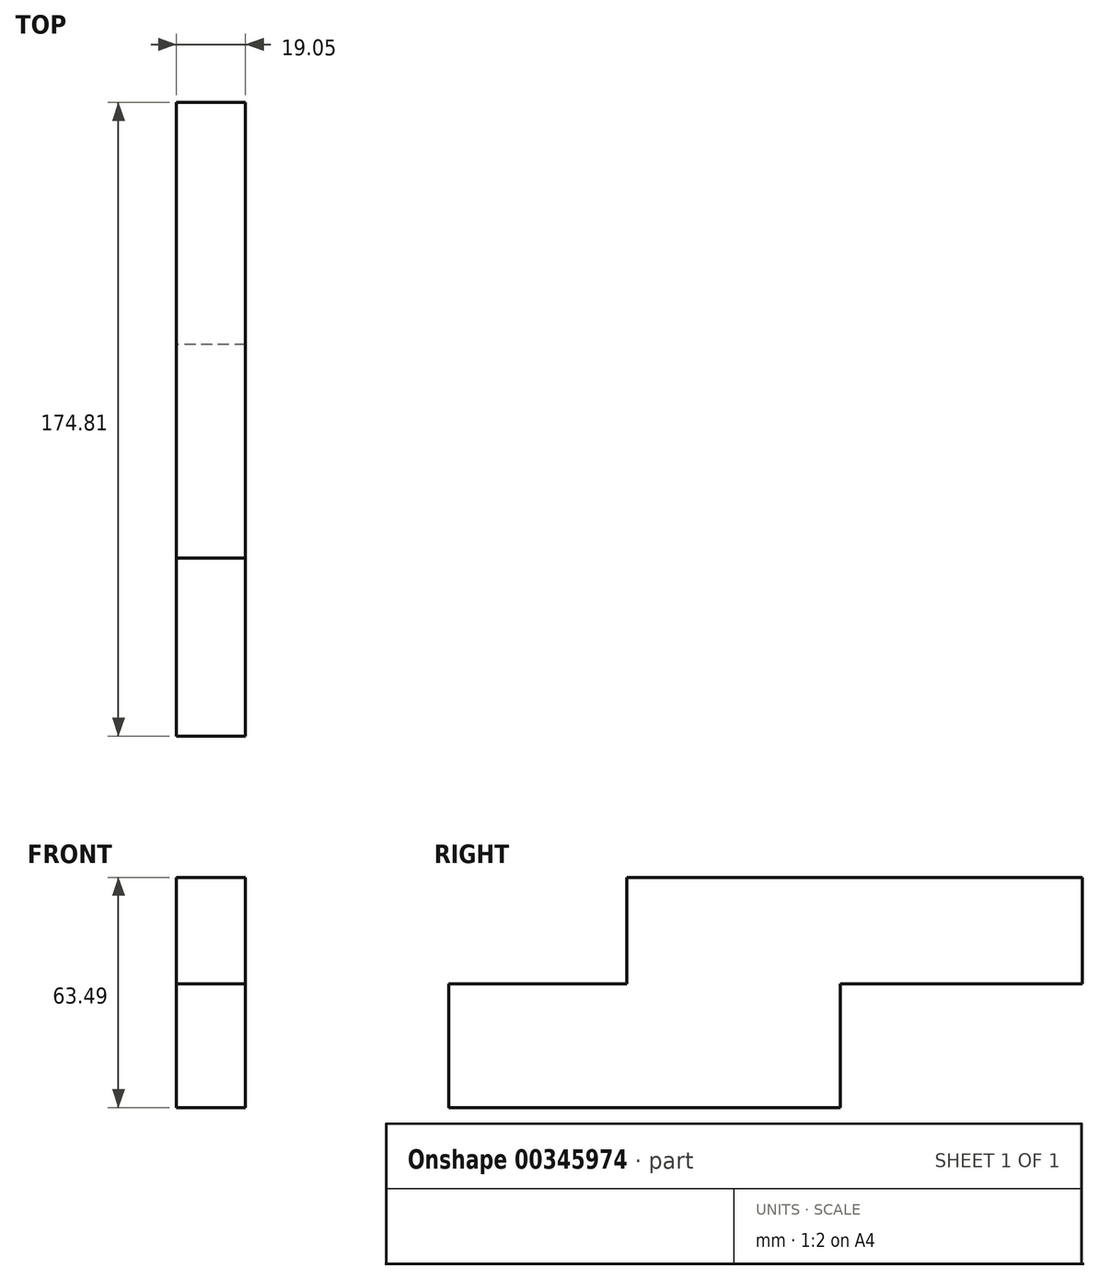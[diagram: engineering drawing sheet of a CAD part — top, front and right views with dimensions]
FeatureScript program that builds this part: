
annotation { "Feature Type Name" : "Feature", "Feature Type Description" : "" }
export const myFeature = defineFeature(function(context is Context, id is Id, definition is map)
    precondition{}
    {
        {
            var Q0;
            Q0=qCreatedBy(makeId("Right.planeOp"),FACE);
            var sketch = newSketch(context, id + "F0", { "sketchPlane" : qUnion([Q0])});
            skLineSegment(sketch, "E0", {"start": v(-49.13, -63.49) * mm, "end": v(74.82, -63.49) * mm});
            skLineSegment(sketch, "E1.bottom", {"start": v(125.68, -29.41) * mm, "end": v(0, -29.41) * mm});
            skLineSegment(sketch, "E1.top", {"start": v(125.68, 0) * mm, "end": v(0, 0) * mm});
            skLineSegment(sketch, "E1.left", {"start": v(125.68, -29.41) * mm, "end": v(125.68, 0) * mm});
            skLineSegment(sketch, "E1.right", {"start": v(0, -29.41) * mm, "end": v(0, 0) * mm});
            skLineSegment(sketch, "E2.bottom", {"start": v(125.68, -63.49) * mm, "end": v(58.93, -63.49) * mm});
            skLineSegment(sketch, "E2.top", {"start": v(125.68, -29.41) * mm, "end": v(58.93, -29.41) * mm});
            skLineSegment(sketch, "E2.left", {"start": v(58.93, -63.49) * mm, "end": v(58.93, -29.41) * mm});
            skLineSegment(sketch, "E2.right", {"start": v(125.68, -63.49) * mm, "end": v(125.68, -29.41) * mm});
            skLineSegment(sketch, "E3.bottom", {"start": v(0, -29.41) * mm, "end": v(-49.13, -29.41) * mm});
            skLineSegment(sketch, "E3.top", {"start": v(0, -63.49) * mm, "end": v(-49.13, -63.49) * mm});
            skLineSegment(sketch, "E3.left", {"start": v(0, -29.41) * mm, "end": v(0, -63.49) * mm});
            skLineSegment(sketch, "E3.right", {"start": v(-49.13, -29.41) * mm, "end": v(-49.13, -63.49) * mm});
            skSolve(sketch);
        }
        {
            var Q0;
            Q0=makeQuery(id+"F0.imprint","IMPRINT",FACE,{"disambiguationData":[TD([[makeQuery(id+"F0.imprint","IMPRINT",EDGE,{"derivedFrom":sQuery(id+"F0.wireOp",EDGE,"E0")}),1.0]])]});
            var Q1;
            Q1=makeQuery(id+"F0.imprint","IMPRINT",FACE,{"disambiguationData":[TD([[makeQuery(id+"F0.imprint","IMPRINT",EDGE,{"derivedFrom":sQuery(id+"F0.wireOp",EDGE,"E1.bottom")}),-1.0]])]});
            var Q2;
            Q2=makeQuery(id+"F0.imprint","IMPRINT",FACE,{"disambiguationData":[TD([[makeQuery(id+"F0.imprint","IMPRINT",EDGE,{"derivedFrom":sQuery(id+"F0.wireOp",EDGE,"E2.top")}),1.0]])]});
            extrude(context, id + "F1", {"entities" : qUnion([Q0, Q1, Q2]), "depth" : 19.05 * mm});
        }
    });
